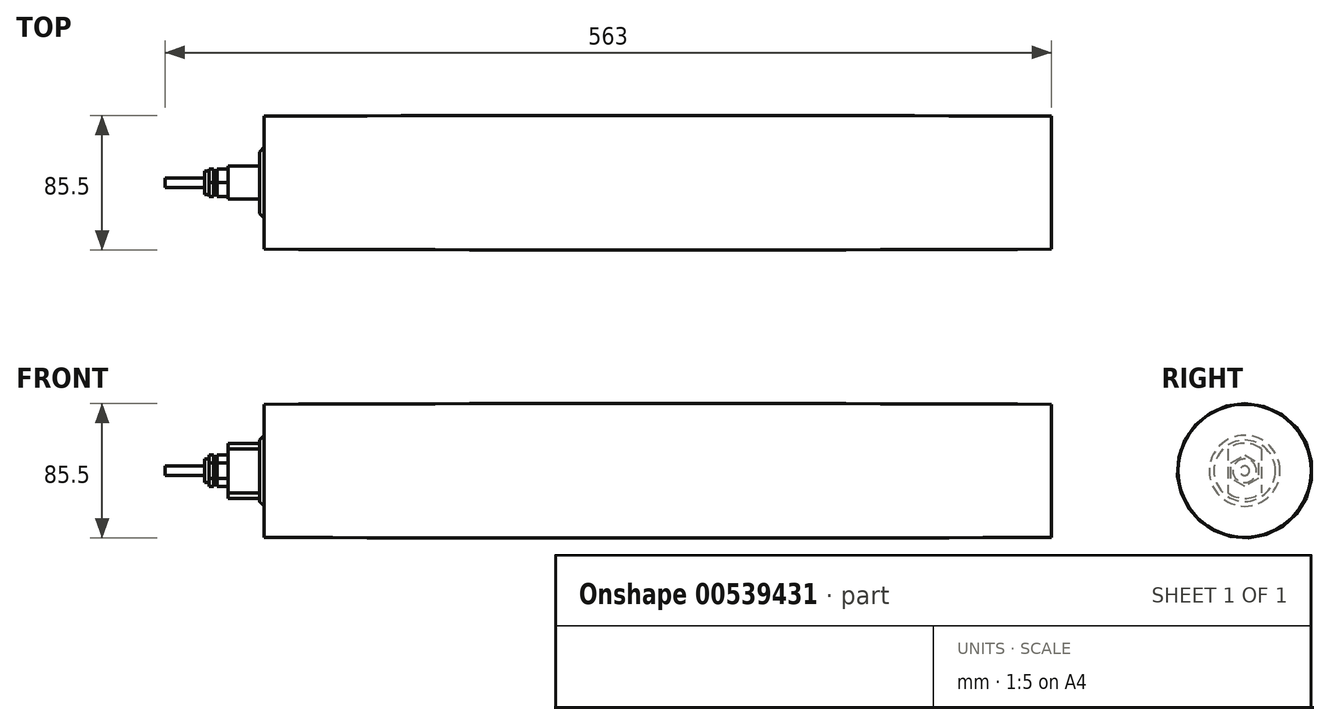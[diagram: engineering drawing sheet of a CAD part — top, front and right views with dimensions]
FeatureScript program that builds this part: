
annotation { "Feature Type Name" : "Feature", "Feature Type Description" : "" }
export const myFeature = defineFeature(function(context is Context, id is Id, definition is map)
    precondition{}
    {
        {
            var Q0;
            Q0=qCreatedBy(makeId("Front.planeOp"),FACE);
            var sketch = newSketch(context, id + "F0", { "sketchPlane" : qUnion([Q0])});
            skLineSegment(sketch, "E0.bottom", {"start": v(-250, 42.25) * mm, "end": v(250, 42.25) * mm});
            skLineSegment(sketch, "E0.top", {"start": v(-250, 0) * mm, "end": v(250, 0) * mm});
            skLineSegment(sketch, "E0.left", {"start": v(-250, 42.25) * mm, "end": v(-250, 0) * mm});
            skLineSegment(sketch, "E0.right", {"start": v(250, 42.25) * mm, "end": v(250, 0) * mm});
            skPoint(sketch, "E0.middle", {"position": v(0, 21.12) * mm});
            skArc(sketch, "E1", {"start": v(250, 42.25) * mm, "mid": v(0, 42.75) * mm, "end": v(-250, 42.25) * mm});
            skSolve(sketch);
        }
        {
            var Q0;
            Q0=makeQuery(id+"F0.imprint","IMPRINT",FACE,{"disambiguationData":[TD([[makeQuery(id+"F0.imprint","IMPRINT",EDGE,{"derivedFrom":sQuery(id+"F0.wireOp",EDGE,"E0.bottom")}),-1.0]])]});
            var Q1;
            Q1=makeQuery(id+"F0.imprint","IMPRINT",FACE,{"disambiguationData":[TD([[makeQuery(id+"F0.imprint","IMPRINT",EDGE,{"derivedFrom":sQuery(id+"F0.wireOp",EDGE,"E0.bottom")}),1.0]])]});
            var Q2;
            Q2=sQuery(id+"F0.wireOp",EDGE,"E0.top");
            revolve(context, id + "F1", {"entities" : qUnion([Q0, Q1]), "axis" : qUnion([Q2]), "revolveType" : RevolveType.FULL});
        }
        {
            var Q0;
            Q0=qCreatedBy(makeId("Front.planeOp"),FACE);
            var sketch = newSketch(context, id + "F2", { "sketchPlane" : qUnion([Q0])});
            skLineSegment(sketch, "E2", {"start": v(-250, 0) * mm, "end": v(-253, 0) * mm});
            skLineSegment(sketch, "E3", {"start": v(-253, 0) * mm, "end": v(-253, 19.5) * mm});
            skLineSegment(sketch, "E4", {"start": v(-253, 19.5) * mm, "end": v(-250, 22.5) * mm});
            skLineSegment(sketch, "E5.0", {"start": v(-250, -42.25) * mm, "end": v(-250, 42.25) * mm});
            skSolve(sketch);
        }
        {
            var Q0;
            {var subQ0=sQuery(id+"F2.wireOp",EDGE,"E2");Q0=makeQuery(id+"F2.imprint","IMPRINT",FACE,{"disambiguationData":[TD([[makeQuery(id+"F2.imprint","IMPRINT",EDGE,{"derivedFrom":subQ0}),-1.0]])]});}
            var Q1;
            Q1=sQuery(id+"F2.wireOp",EDGE,"E2");
            revolve(context, id + "F3", {"operationType" : NewBodyOperationType.ADD, "entities" : qUnion([Q0]), "axis" : qUnion([Q1]), "revolveType" : RevolveType.FULL});
        }
        {
            var Q0;
            Q0=makeQuery(id+"F3.opRevolve","SWEPT_FACE",FACE,{"disambiguationData":[OSD([sQuery(id+"F2.wireOp",EDGE,"E3")])]});
            var sketch = newSketch(context, id + "F4", { "sketchPlane" : qUnion([Q0])});
            skLineSegment(sketch, "E6.bottom", {"start": v(-10.5, 14) * mm, "end": v(10.5, 14) * mm});
            skLineSegment(sketch, "E6.top", {"start": v(-10.5, -14) * mm, "end": v(10.5, -14) * mm});
            skLineSegment(sketch, "E6.left", {"start": v(-10.5, 14) * mm, "end": v(-10.5, -14) * mm});
            skLineSegment(sketch, "E6.right", {"start": v(10.5, 14) * mm, "end": v(10.5, -14) * mm});
            skPoint(sketch, "E6.middle", {"position": v(0, 0) * mm});
            skArc(sketch, "E7", {"start": v(10.5, 14) * mm, "mid": v(0, 17.5) * mm, "end": v(-10.5, 14) * mm});
            skArc(sketch, "E8", {"start": v(-10.5, -14) * mm, "mid": v(0, -17.5) * mm, "end": v(10.5, -14) * mm});
            skSolve(sketch);
        }
        {
            var Q0;
            Q0=makeQuery(id+"F4.imprint","IMPRINT",FACE,{"disambiguationData":[TD([[makeQuery(id+"F4.imprint","IMPRINT",EDGE,{"derivedFrom":sQuery(id+"F4.wireOp",EDGE,"E6.bottom")}),-1.0]])]});
            var Q1;
            Q1=makeQuery(id+"F4.imprint","IMPRINT",FACE,{"disambiguationData":[TD([[makeQuery(id+"F4.imprint","IMPRINT",EDGE,{"derivedFrom":sQuery(id+"F4.wireOp",EDGE,"E6.bottom")}),1.0]])]});
            var Q2;
            Q2=makeQuery(id+"F4.imprint","IMPRINT",FACE,{"disambiguationData":[TD([[makeQuery(id+"F4.imprint","IMPRINT",EDGE,{"derivedFrom":sQuery(id+"F4.wireOp",EDGE,"E6.top")}),-1.0]])]});
            extrude(context, id + "F5", {"entities" : qUnion([Q0, Q1, Q2]), "operationType" : NewBodyOperationType.ADD, "depth" : 20 * mm, "offsetDistance" : 25 * mm});
        }
        {
            var Q0;
            Q0=makeQuery(id+"F5.opExtrude","CAP_FACE",FACE,{"disambiguationData":[OSD([sQuery(id+"F4.wireOp",EDGE,"E6.left"),sQuery(id+"F4.wireOp",EDGE,"E6.right"),sQuery(id+"F4.wireOp",EDGE,"E7"),sQuery(id+"F4.wireOp",EDGE,"E8")])],"isStart":false});
            var sketch = newSketch(context, id + "F6", { "sketchPlane" : qUnion([Q0])});
            skCircle(sketch, "E9.cCircle", {"center": v(0, 0) * mm, "radius": 8.66 * mm, "construction": true});
            skLineSegment(sketch, "E9.0", {"start": v(-8.66, 5) * mm, "end": v(0, 10) * mm});
            skLineSegment(sketch, "E9.1", {"start": v(0, 10) * mm, "end": v(8.66, 5) * mm});
            skLineSegment(sketch, "E9.2", {"start": v(8.66, 5) * mm, "end": v(8.66, -5) * mm});
            skLineSegment(sketch, "E9.3", {"start": v(8.66, -5) * mm, "end": v(0, -10) * mm});
            skLineSegment(sketch, "E9.4", {"start": v(0, -10) * mm, "end": v(-8.66, -5) * mm});
            skLineSegment(sketch, "E9.5", {"start": v(-8.66, -5) * mm, "end": v(-8.66, 5) * mm});
            skPoint(sketch, "E9.0.midPoint", {"position": v(-4.33, 7.5) * mm});
            skLineSegment(sketch, "E10", {"start": v(0, 10) * mm, "end": v(0, -10) * mm, "construction": true});
            skSolve(sketch);
        }
        {
            var Q0;
            Q0=makeQuery(id+"F6.imprint","IMPRINT",FACE,{"disambiguationData":[TD([[makeQuery(id+"F6.imprint","IMPRINT",EDGE,{"derivedFrom":sQuery(id+"F6.wireOp",EDGE,"E9.0")}),-1.0]])]});
            extrude(context, id + "F7", {"entities" : qUnion([Q0]), "operationType" : NewBodyOperationType.ADD, "depth" : 15 * mm, "offsetDistance" : 25 * mm});
        }
        {
            var Q0;
            Q0=makeQuery(id+"F7.opExtrude","CAP_FACE",FACE,{"disambiguationData":[OSD([sQuery(id+"F6.wireOp",EDGE,"E9.0"),sQuery(id+"F6.wireOp",EDGE,"E9.1"),sQuery(id+"F6.wireOp",EDGE,"E9.2"),sQuery(id+"F6.wireOp",EDGE,"E9.3"),sQuery(id+"F6.wireOp",EDGE,"E9.4"),sQuery(id+"F6.wireOp",EDGE,"E9.5")])],"isStart":false});
            var sketch = newSketch(context, id + "F8", { "sketchPlane" : qUnion([Q0])});
            skLineSegment(sketch, "E11.0.0", {"start": v(-8.66, 5) * mm, "end": v(-8.66, -5) * mm});
            skLineSegment(sketch, "E11.0.1", {"start": v(-8.66, -5) * mm, "end": v(0, -10) * mm});
            skLineSegment(sketch, "E11.0.2", {"start": v(0, -10) * mm, "end": v(8.66, -5) * mm});
            skLineSegment(sketch, "E11.0.3", {"start": v(8.66, -5) * mm, "end": v(8.66, 5) * mm});
            skLineSegment(sketch, "E11.0.4", {"start": v(8.66, 5) * mm, "end": v(0, 10) * mm});
            skLineSegment(sketch, "E11.0.5", {"start": v(0, 10) * mm, "end": v(-8.66, 5) * mm});
            skCircle(sketch, "E12", {"center": v(0, 0) * mm, "radius": 7.5 * mm});
            skSolve(sketch);
        }
        {
            var Q0;
            Q0=makeQuery(id+"F8.imprint","IMPRINT",FACE,{"disambiguationData":[TD([[makeQuery(id+"F8.imprint","IMPRINT",EDGE,{"derivedFrom":sQuery(id+"F8.wireOp",EDGE,"E11.0.0")}),-1.0]])]});
            extrude(context, id + "F9", {"entities" : qUnion([Q0]), "operationType" : NewBodyOperationType.REMOVE, "oppositeDirection" : true, "depth" : 3 * mm, "offsetDistance" : 25 * mm});
        }
        {
            var Q0;
            Q0=qCreatedBy(makeId("Front.planeOp"),FACE);
            var sketch = newSketch(context, id + "F10", { "sketchPlane" : qUnion([Q0])});
            skLineSegment(sketch, "E13.0", {"start": v(-285, 10) * mm, "end": v(-273, 10) * mm});
            skLineSegment(sketch, "E14.bottom", {"start": v(-282, 10) * mm, "end": v(-280, 10) * mm});
            skLineSegment(sketch, "E14.top", {"start": v(-282, 7.5) * mm, "end": v(-280, 7.5) * mm});
            skLineSegment(sketch, "E14.left", {"start": v(-282, 10) * mm, "end": v(-282, 7.5) * mm});
            skLineSegment(sketch, "E14.right", {"start": v(-280, 10) * mm, "end": v(-280, 7.5) * mm});
            skPoint(sketch, "E14.middle", {"position": v(-281, 8.75) * mm});
            skLineSegment(sketch, "E15", {"start": v(-288, 7.5) * mm, "end": v(-285, 7.5) * mm});
            skLineSegment(sketch, "E16", {"start": v(0, 0) * mm, "end": v(-20, 0) * mm, "construction": true});
            skSolve(sketch);
        }
        {
            var Q0;
            Q0 = qSketchRegion(id + "F10", true);
            var Q1;
            Q1=sQuery(id+"F10.wireOp",EDGE,"E16");
            revolve(context, id + "F11", {"operationType" : NewBodyOperationType.REMOVE, "entities" : qUnion([Q0]), "axis" : qUnion([Q1]), "revolveType" : RevolveType.FULL, "oppositeDirection" : true});
        }
        {
            var Q0;
            Q0=makeQuery(id+"F7.opExtrude","CAP_FACE",FACE,{"disambiguationData":[OSD([sQuery(id+"F6.wireOp",EDGE,"E9.0"),sQuery(id+"F6.wireOp",EDGE,"E9.1"),sQuery(id+"F6.wireOp",EDGE,"E9.2"),sQuery(id+"F6.wireOp",EDGE,"E9.3"),sQuery(id+"F6.wireOp",EDGE,"E9.4"),sQuery(id+"F6.wireOp",EDGE,"E9.5")])],"isStart":false});
            var sketch = newSketch(context, id + "F12", { "sketchPlane" : qUnion([Q0])});
            skCircle(sketch, "E17", {"center": v(0, 0) * mm, "radius": 3 * mm});
            skSolve(sketch);
        }
        {
            var Q0;
            Q0=makeQuery(id+"F12.imprint","IMPRINT",FACE,{"disambiguationData":[TD([[makeQuery(id+"F12.imprint","IMPRINT",EDGE,{"derivedFrom":sQuery(id+"F12.wireOp",EDGE,"E17")}),1.0]])]});
            extrude(context, id + "F13", {"entities" : qUnion([Q0]), "operationType" : NewBodyOperationType.ADD, "depth" : 25 * mm, "offsetDistance" : 25 * mm});
        }
    });
